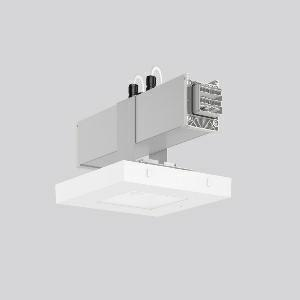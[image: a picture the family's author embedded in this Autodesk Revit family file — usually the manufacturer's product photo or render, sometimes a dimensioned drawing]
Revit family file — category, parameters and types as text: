
# Revit family: linedo_module_rf_9503rf_760_409_00a_4744
name_source: partatom
category: Lighting Fixtures
units: mm (PartAtom-declared; Revit-internal decimal feet)

## family parameters
Cut with Voids When Loaded = No
Host = Face
Light Source = No
Part Type = Normal
Room Calculation Point = No
Round Connector Dimension = Use Diameter
Shared = No

## types (1)
- LINEDO Module RF (1 x LED Modul 765, 420 lm, 6500)
    Apparent Load = 7 VA
    Approval mark = CE
    CIE Flux Codes = 48 88 100 100 100
    Color Rendering = 70
    Color Temperature = 6500
    Default Elevation = 1800 mm
    Description = LINEDO, 6,7 W, 420 lm, 765, silver, on/off
Continuous line luminaire, L 330 B 198 H 170, CBS, emergency-420 lm
    Height = 170 mm  [stored 0.557743 ft]
    Lamp = 1 x LED Modul 765
    Lamp Light Flux = 420 lm
    Lamp count = 1
    Length = 330 mm
    Lifetime = 50000 h
    Luminous efficacy = 63 lm/W
    Manufacturer = RZB
    ModVariant = No
    Model = 9503RF.760.409.00A
    Mounting Place = Ceiling
    Mounting Type = Surface mounted
    Number of Poles = 1
    OnlyDefault = Yes
    Power Factor = 1
    Product Name = LINEDO Module RF
    Product group = Continuous line luminaire system Linedo IP 54
    ProductGroupID = 314
    Protection Class = Protection class I
    Protection Degree = IP 54
    RLX_Detail_Level = 1
    RLX_Emergency_Light_Flux = 420 lm
    RLX_Emergency_Type = 3
    RLX_Emergency_Type_DB = Yes
    RlxData = <blob elided: 21649 chars, md5=1f3955fc>
    Socket = socket
    Standby Power = 0 W
    System Light Flux = 420 lm
    System Power = 7 W
    Type Comments = Product without accessories
    Type Image = 9503rw.760.434.000.jpg
    URL = http://relux.com
    VarID = ---
    Voltage = 230 V
    Voltage Range = 220-240 V
    Weight = 0.00 kg
    Width = 198 mm

note: [stored X ft] marks values corroborated as IEEE doubles in the binary element streams (Revit-internal decimal feet)

## geometry (parser evidence)
native form markers: Blend x4, Sweep x15
no freeform markers — native parametric forms only
